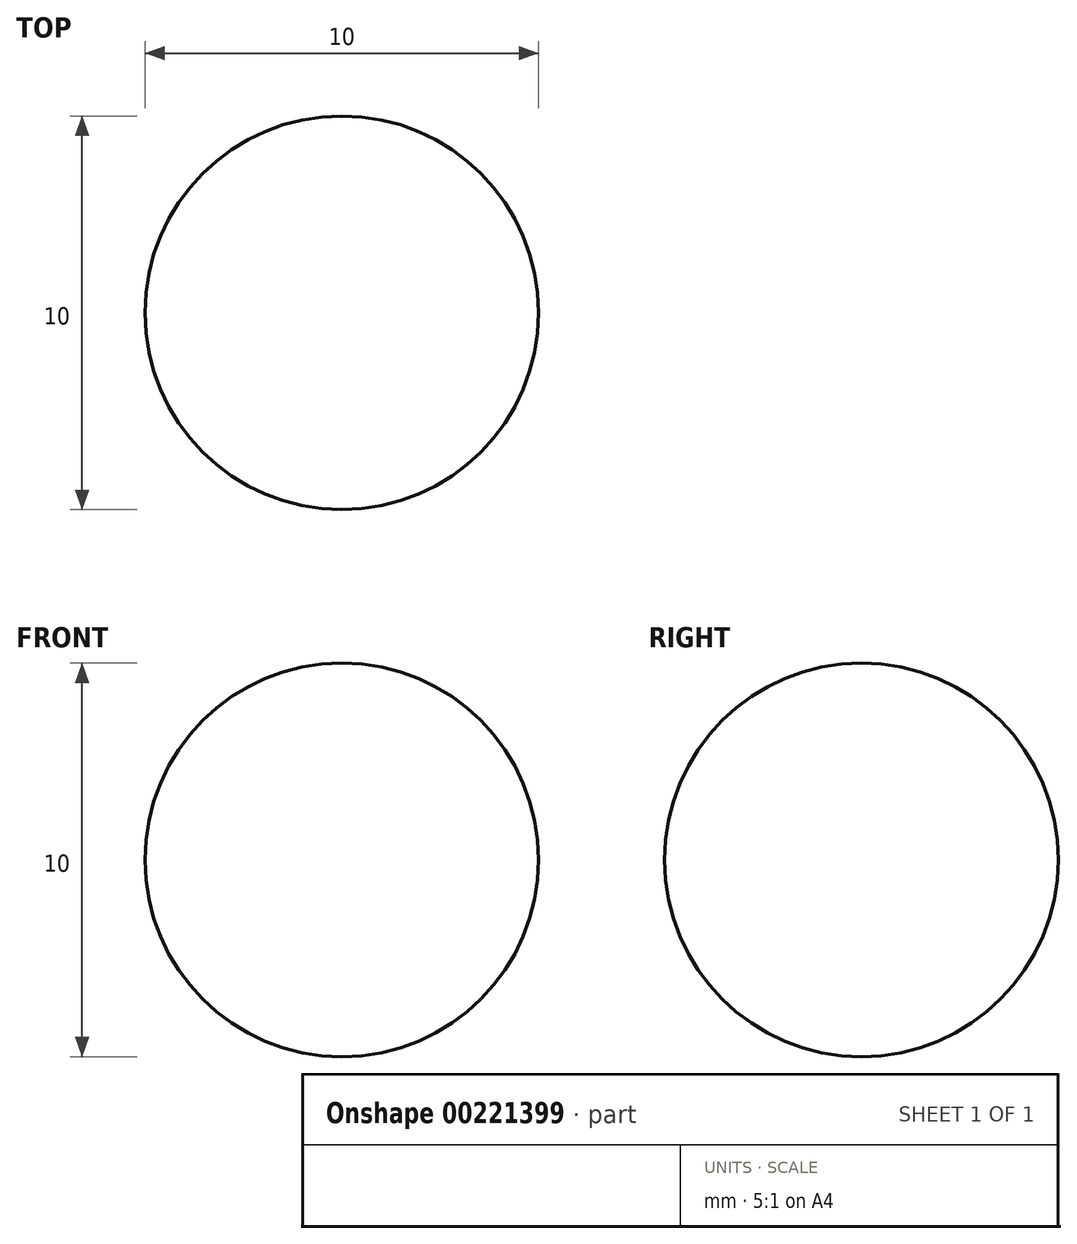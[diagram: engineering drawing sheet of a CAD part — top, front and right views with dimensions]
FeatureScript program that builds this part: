
annotation { "Feature Type Name" : "Feature", "Feature Type Description" : "" }
export const myFeature = defineFeature(function(context is Context, id is Id, definition is map)
    precondition{}
    {
        {
            var Q0;
            Q0=qCreatedBy(makeId("Front.planeOp"),FACE);
            var sketch = newSketch(context, id + "F0", { "sketchPlane" : qUnion([Q0])});
            skArc(sketch, "E0", {"start": v(5, 0) * mm, "mid": v(0, 5) * mm, "end": v(-5, 0) * mm});
            skLineSegment(sketch, "E1", {"start": v(-5, 0) * mm, "end": v(5, 0) * mm});
            skSolve(sketch);
        }
        {
            var Q0;
            Q0=makeQuery(id+"F0.imprint","IMPRINT",FACE,{"disambiguationData":[TD([[makeQuery(id+"F0.imprint","IMPRINT",EDGE,{"derivedFrom":sQuery(id+"F0.wireOp",EDGE,"E0")}),1.0]])]});
            var Q1;
            Q1=sQuery(id+"F0.wireOp",EDGE,"E1");
            revolve(context, id + "F1", {"entities" : qUnion([Q0]), "axis" : qUnion([Q1]), "revolveType" : RevolveType.FULL});
        }
    });
